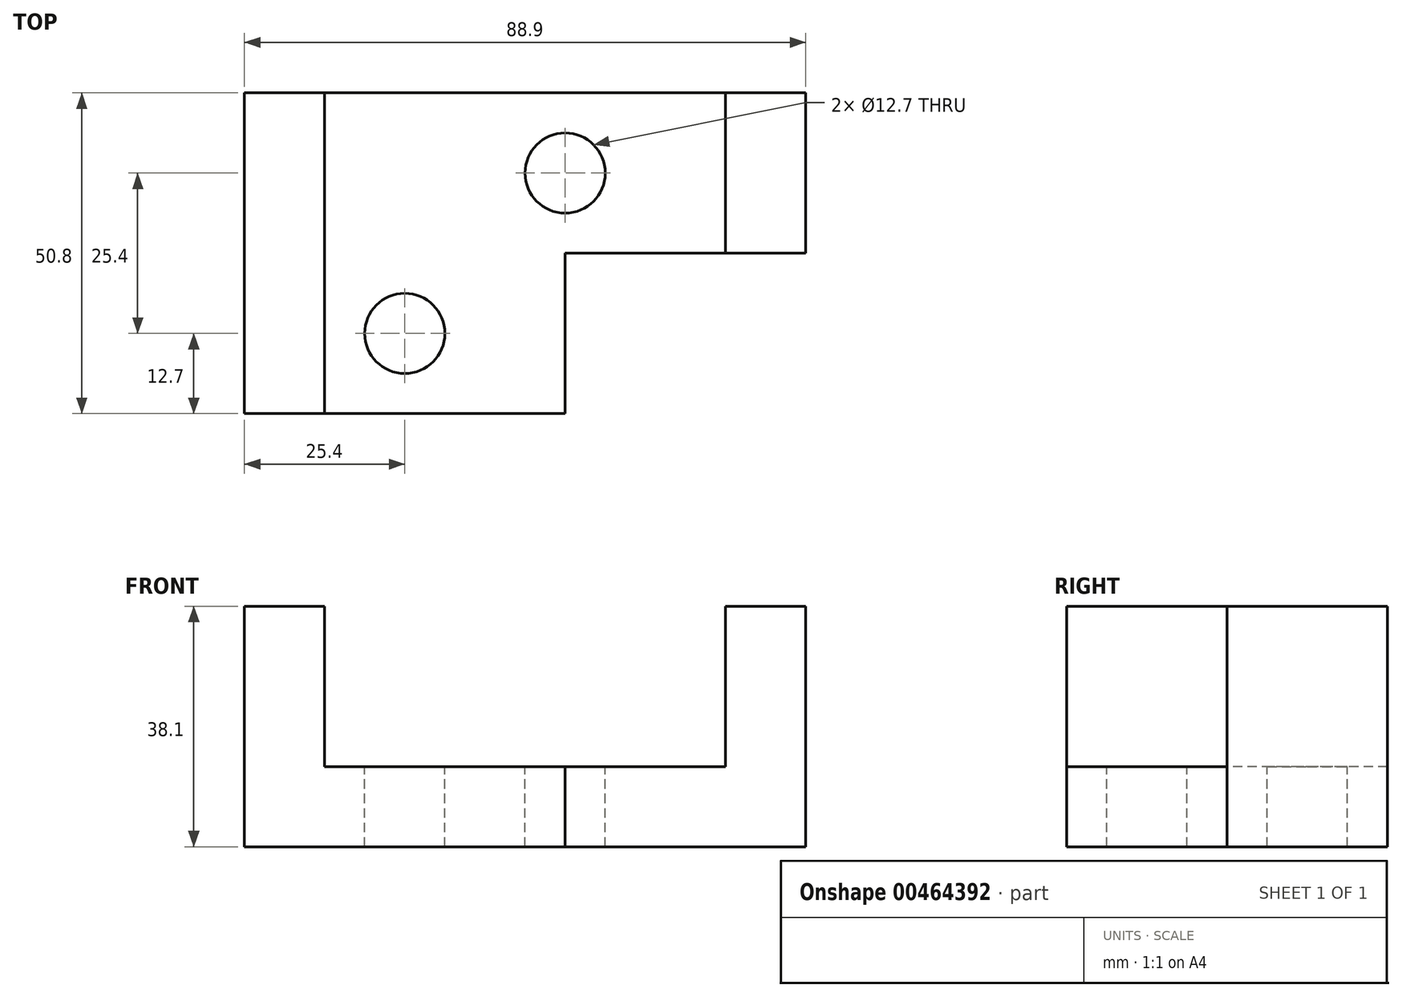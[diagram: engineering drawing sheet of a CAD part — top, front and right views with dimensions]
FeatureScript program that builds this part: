
annotation { "Feature Type Name" : "Feature", "Feature Type Description" : "" }
export const myFeature = defineFeature(function(context is Context, id is Id, definition is map)
    precondition{}
    {
        {
            var Q0;
            Q0=qCreatedBy(makeId("Front.planeOp"),FACE);
            var sketch = newSketch(context, id + "F0", { "sketchPlane" : qUnion([Q0])});
            skLineSegment(sketch, "E0.bottom", {"start": v(44.45, -19.05) * mm, "end": v(-44.45, -19.05) * mm});
            skLineSegment(sketch, "E0.top", {"start": v(44.45, 19.05) * mm, "end": v(-44.45, 19.05) * mm});
            skLineSegment(sketch, "E0.left", {"start": v(44.45, -19.05) * mm, "end": v(44.45, 19.05) * mm});
            skLineSegment(sketch, "E0.right", {"start": v(-44.45, -19.05) * mm, "end": v(-44.45, 19.05) * mm});
            skPoint(sketch, "E0.middle", {"position": v(0, 0) * mm});
            skSolve(sketch);
        }
        {
            var Q0;
            Q0 = qSketchRegion(id + "F0", true);
            extrude(context, id + "F1", {"entities" : qUnion([Q0]), "depth" : 50.8 * mm});
        }
        {
            var Q0;
            Q0=makeQuery(id+"F1.opExtrude","CAP_FACE",FACE,{"disambiguationData":[OSD([sQuery(id+"F0.wireOp",EDGE,"E0.bottom"),sQuery(id+"F0.wireOp",EDGE,"E0.top"),sQuery(id+"F0.wireOp",EDGE,"E0.left"),sQuery(id+"F0.wireOp",EDGE,"E0.right")])],"isStart":false});
            var sketch = newSketch(context, id + "F2", { "sketchPlane" : qUnion([Q0])});
            skLineSegment(sketch, "E1.bottom", {"start": v(-31.75, 19.05) * mm, "end": v(31.75, 19.05) * mm});
            skLineSegment(sketch, "E1.top", {"start": v(-31.75, -6.35) * mm, "end": v(31.75, -6.35) * mm});
            skLineSegment(sketch, "E1.left", {"start": v(-31.75, 19.05) * mm, "end": v(-31.75, -6.35) * mm});
            skLineSegment(sketch, "E1.right", {"start": v(31.75, 19.05) * mm, "end": v(31.75, -6.35) * mm});
            skSolve(sketch);
        }
        {
            var Q0;
            Q0 = qSketchRegion(id + "F2", true);
            extrude(context, id + "F3", {"entities" : qUnion([Q0]), "operationType" : NewBodyOperationType.REMOVE, "endBound" : BoundingType.THROUGH_ALL, "oppositeDirection" : true, "depth" : 25.4 * mm});
        }
        {
            var Q0;
            {var subQ1=sQuery(id+"F0.wireOp",EDGE,"E0.left");var subQ2=sQuery(id+"F0.wireOp",EDGE,"E0.top");Q0=makeQuery(id+"F3.boolean.opBoolean","SPLIT",FACE,{"disambiguationData":[TD([makeQuery(id+"F1.opExtrude","SWEPT_FACE",FACE,{"disambiguationData":[OSD([subQ1])]})])],"derivedFrom":makeQuery(id+"F1.opExtrude","SWEPT_FACE",FACE,{"disambiguationData":[OSD([subQ2])]})});}
            var sketch = newSketch(context, id + "F4", { "sketchPlane" : qUnion([Q0])});
            skLineSegment(sketch, "E2.bottom", {"start": v(44.45, -50.8) * mm, "end": v(6.35, -50.8) * mm});
            skLineSegment(sketch, "E2.top", {"start": v(44.45, -25.4) * mm, "end": v(6.35, -25.4) * mm});
            skLineSegment(sketch, "E2.left", {"start": v(44.45, -50.8) * mm, "end": v(44.45, -25.4) * mm});
            skLineSegment(sketch, "E2.right", {"start": v(6.35, -50.8) * mm, "end": v(6.35, -25.4) * mm});
            skSolve(sketch);
        }
        {
            var Q0;
            Q0 = qSketchRegion(id + "F4", true);
            extrude(context, id + "F5", {"entities" : qUnion([Q0]), "operationType" : NewBodyOperationType.REMOVE, "endBound" : BoundingType.THROUGH_ALL, "oppositeDirection" : true, "depth" : 25.4 * mm});
        }
        {
            var Q0;
            Q0=makeQuery(id+"F3.boolean.opBoolean","COPY",FACE,{"derivedFrom":makeQuery(id+"F3.opExtrude","SWEPT_FACE",FACE,{"disambiguationData":[OSD([sQuery(id+"F2.wireOp",EDGE,"E1.top")])]})});
            var sketch = newSketch(context, id + "F6", { "sketchPlane" : qUnion([Q0])});
            skCircle(sketch, "E3", {"center": v(6.35, -12.7) * mm, "radius": 6.35 * mm});
            skSolve(sketch);
        }
        {
            var Q0;
            Q0 = qSketchRegion(id + "F6", true);
            extrude(context, id + "F7", {"entities" : qUnion([Q0]), "operationType" : NewBodyOperationType.REMOVE, "endBound" : BoundingType.THROUGH_ALL, "oppositeDirection" : true, "depth" : 25.4 * mm});
        }
        {
            var Q0;
            Q0=makeQuery(id+"F3.boolean.opBoolean","COPY",FACE,{"derivedFrom":makeQuery(id+"F3.opExtrude","SWEPT_FACE",FACE,{"disambiguationData":[OSD([sQuery(id+"F2.wireOp",EDGE,"E1.top")])]})});
            var sketch = newSketch(context, id + "F8", { "sketchPlane" : qUnion([Q0])});
            skCircle(sketch, "E4", {"center": v(-19.05, -38.1) * mm, "radius": 6.35 * mm});
            skSolve(sketch);
        }
        {
            var Q0;
            Q0 = qSketchRegion(id + "F8", true);
            extrude(context, id + "F9", {"entities" : qUnion([Q0]), "operationType" : NewBodyOperationType.REMOVE, "endBound" : BoundingType.THROUGH_ALL, "oppositeDirection" : true, "depth" : 25.4 * mm});
        }
    });
